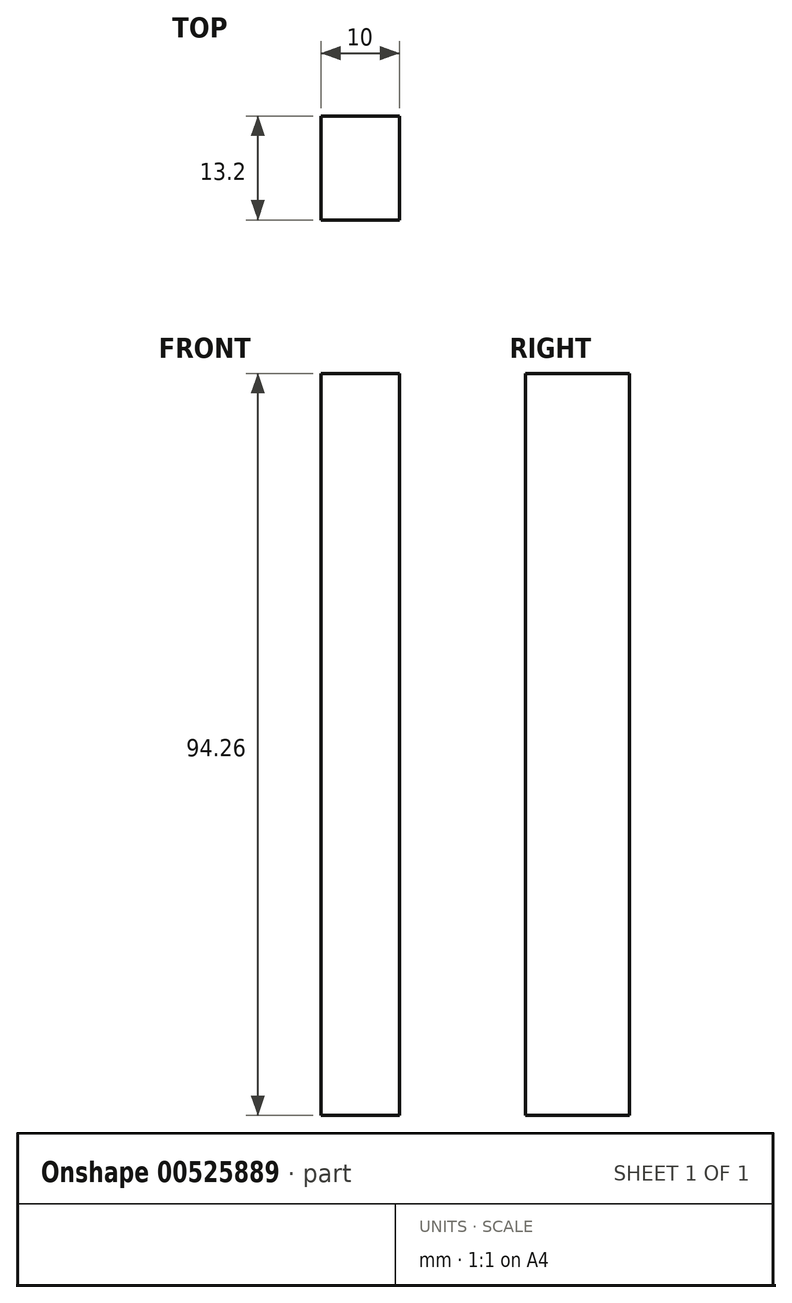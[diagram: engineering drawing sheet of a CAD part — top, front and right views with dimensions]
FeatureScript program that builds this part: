
annotation { "Feature Type Name" : "Feature", "Feature Type Description" : "" }
export const myFeature = defineFeature(function(context is Context, id is Id, definition is map)
    precondition{}
    {
        {
            var Q0;
            Q0=qCreatedBy(makeId("Right.planeOp"),FACE);
            var sketch = newSketch(context, id + "F0", { "sketchPlane" : qUnion([Q0])});
            skLineSegment(sketch, "E0.bottom", {"start": v(-203.32, 86.22) * mm, "end": v(-190.12, 86.22) * mm});
            skLineSegment(sketch, "E0.top", {"start": v(-203.32, -8.04) * mm, "end": v(-190.12, -8.04) * mm});
            skLineSegment(sketch, "E0.left", {"start": v(-203.32, 86.22) * mm, "end": v(-203.32, -8.04) * mm});
            skLineSegment(sketch, "E0.right", {"start": v(-190.12, 86.22) * mm, "end": v(-190.12, -8.04) * mm});
            skSolve(sketch);
        }
        {
            var Q0;
            Q0 = qSketchRegion(id + "F0", true);
            extrude(context, id + "F1", {"entities" : qUnion([Q0]), "depth" : 10 * mm, "offsetDistance" : 25 * mm});
        }
    });
